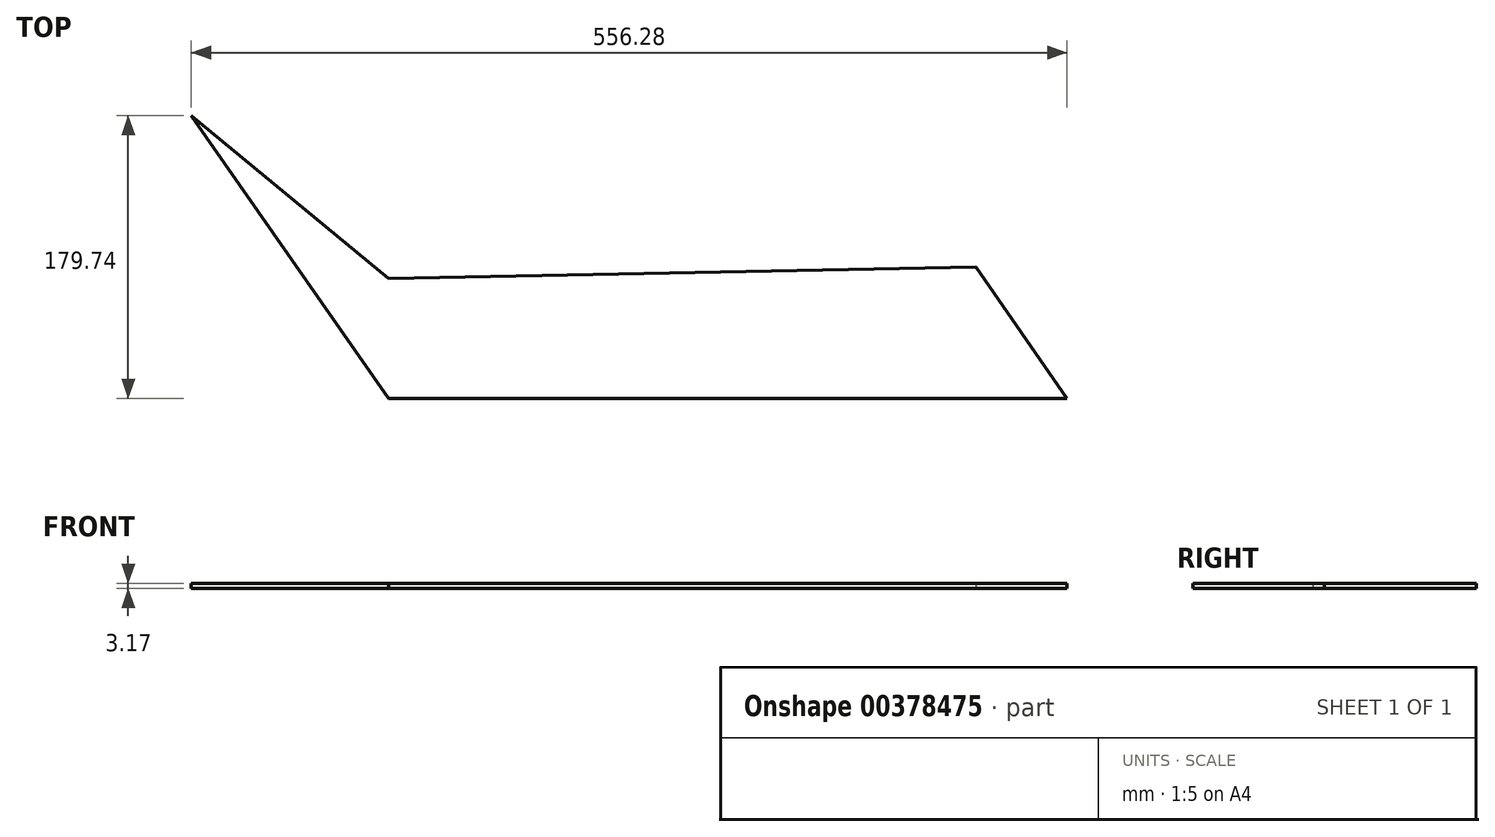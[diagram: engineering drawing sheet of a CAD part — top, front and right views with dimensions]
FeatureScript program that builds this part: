
annotation { "Feature Type Name" : "Feature", "Feature Type Description" : "" }
export const myFeature = defineFeature(function(context is Context, id is Id, definition is map)
    precondition{}
    {
        {
            var Q0;
            Q0=qCreatedBy(makeId("Top.planeOp"),FACE);
            var sketch = newSketch(context, id + "F0", { "sketchPlane" : qUnion([Q0])});
            skLineSegment(sketch, "E0.bottom", {"start": v(-186.48, 34.52) * mm, "end": v(186.48, 41.68) * mm});
            skPoint(sketch, "E0.middle", {"position": v(0, 0) * mm});
            skLineSegment(sketch, "E1", {"start": v(-186.48, -41.68) * mm, "end": v(-311.72, 138.06) * mm});
            skLineSegment(sketch, "E2", {"start": v(-311.72, 138.06) * mm, "end": v(-186.48, 34.52) * mm});
            skLineSegment(sketch, "E3", {"start": v(186.48, 41.68) * mm, "end": v(244.56, -41.68) * mm});
            skLineSegment(sketch, "E4", {"start": v(-186.48, -41.68) * mm, "end": v(244.56, -41.68) * mm});
            skSolve(sketch);
        }
        {
            var Q0;
            Q0 = qSketchRegion(id + "F0", true);
            extrude(context, id + "F1", {"entities" : qUnion([Q0]), "depth" : 3.17 * mm});
        }
    });
